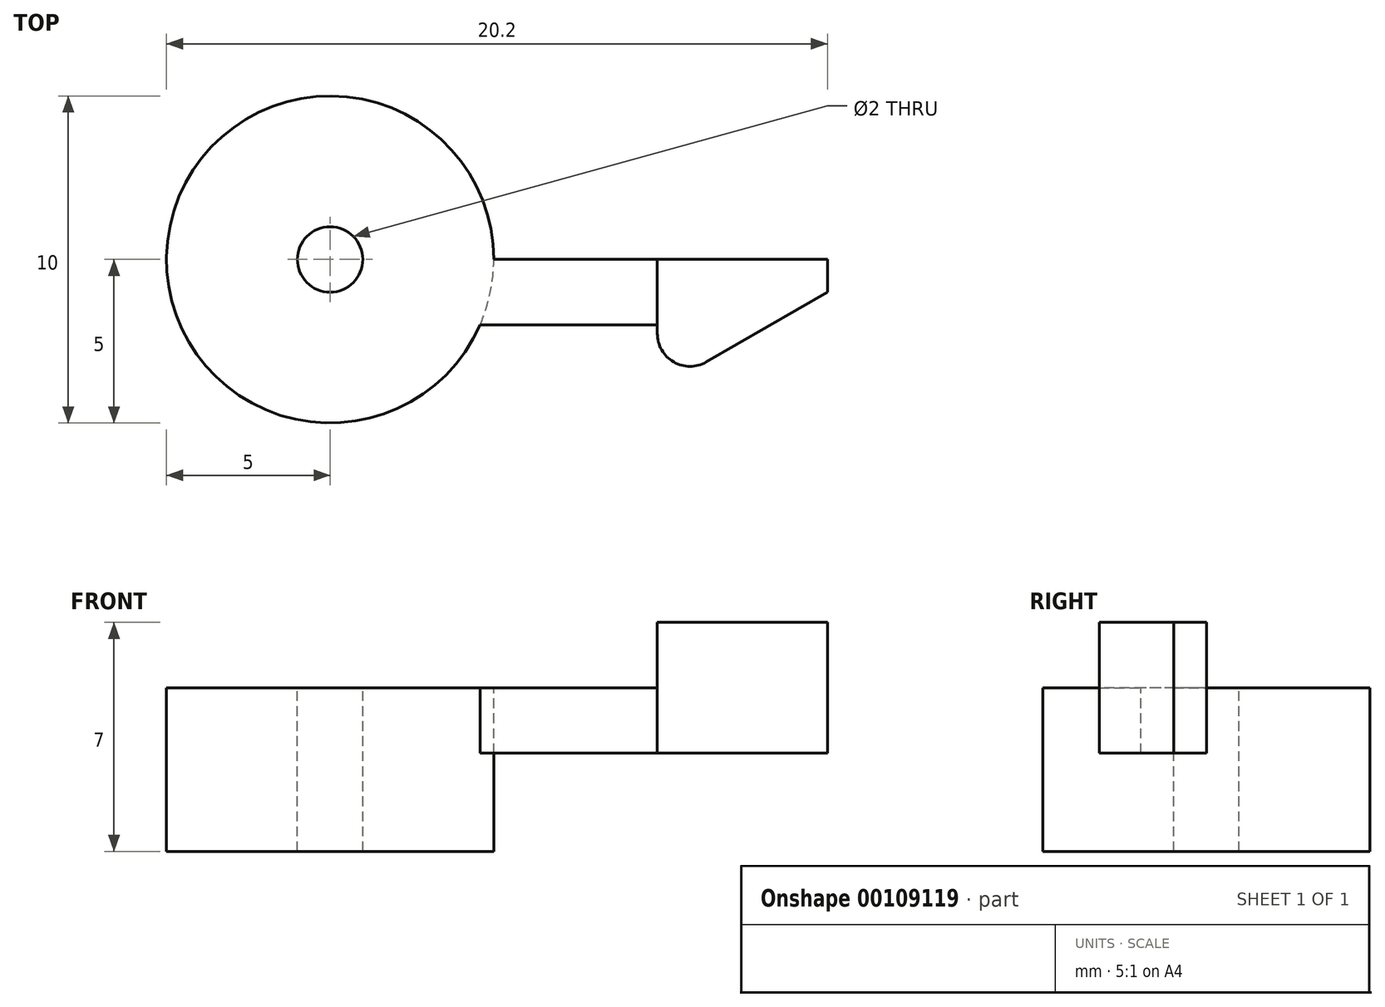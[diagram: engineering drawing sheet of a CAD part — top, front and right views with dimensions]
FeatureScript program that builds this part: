
annotation { "Feature Type Name" : "Feature", "Feature Type Description" : "" }
export const myFeature = defineFeature(function(context is Context, id is Id, definition is map)
    precondition{}
    {
        {
            var Q0;
            Q0=qCreatedBy(makeId("Top.planeOp"),FACE);
            var sketch = newSketch(context, id + "F0", { "sketchPlane" : qUnion([Q0])});
            skCircle(sketch, "E0", {"center": v(0, 0) * mm, "radius": 5 * mm});
            skLineSegment(sketch, "E1.MirrorCS", {"start": v(10, -2) * mm, "end": v(4.58, -2) * mm});
            skLineSegment(sketch, "E2.MirrorCS", {"start": v(10, -4) * mm, "end": v(15.2, -1) * mm});
            skLineSegment(sketch, "E3.MirrorCS", {"start": v(10, -2) * mm, "end": v(10, -4) * mm});
            skLineSegment(sketch, "E4.MirrorCS", {"start": v(15.2, -1) * mm, "end": v(15.2, 0) * mm});
            skLineSegment(sketch, "E5.MirrorCS", {"start": v(10, 0) * mm, "end": v(10, -2) * mm});
            skLineSegment(sketch, "E6", {"start": v(15.2, 0) * mm, "end": v(5, 0) * mm});
            skSolve(sketch);
        }
        {
            var Q0;
            {var subQ0=sQuery(id+"F0.wireOp",EDGE,"E0");var subQ1=makeQuery(id+"F0.imprint","INTERSECT",VERTEX,{"derivedFrom":[subQ0,sQuery(id+"F0.wireOp",EDGE,"E1.MirrorCS")]});Q0=makeQuery(id+"F0.imprint","IMPRINT",FACE,{"disambiguationData":[TD([[makeQuery(id+"F0.imprint","IMPRINT",EDGE,{"disambiguationData":[TD([[subQ1,1.0]])],"derivedFrom":subQ0}),1.0]])]});}
            extrude(context, id + "F1", {"entities" : qUnion([Q0]), "oppositeDirection" : true, "depth" : 5 * mm});
        }
        {
            var Q0;
            {var subQ0=sQuery(id+"F0.wireOp",EDGE,"E1.MirrorCS");Q0=makeQuery(id+"F0.imprint","IMPRINT",FACE,{"disambiguationData":[TD([[makeQuery(id+"F0.imprint","IMPRINT",EDGE,{"derivedFrom":subQ0}),-1.0]])]});}
            extrude(context, id + "F2", {"entities" : qUnion([Q0]), "operationType" : NewBodyOperationType.ADD, "oppositeDirection" : true, "depth" : 2 * mm});
        }
        {
            var Q0;
            Q0=makeQuery(id+"F0.imprint","IMPRINT",FACE,{"disambiguationData":[TD([[makeQuery(id+"F0.imprint","IMPRINT",EDGE,{"derivedFrom":sQuery(id+"F0.wireOp",EDGE,"E2.MirrorCS")}),1.0]])]});
            extrude(context, id + "F3", {"entities" : qUnion([Q0]), "operationType" : NewBodyOperationType.ADD, "endBound" : BoundingType.SYMMETRIC, "depth" : 4 * mm});
        }
        {
            var Q0;
            Q0=makeQuery(id+"F3.opExtrude","SWEPT_EDGE",EDGE,{"disambiguationData":[OSD([sQuery(id+"F0.wireOp",EDGE,"E2.MirrorCS"),sQuery(id+"F0.wireOp",EDGE,"E3.MirrorCS")])]});
            fillet(context, id + "F4", {"entities" : qUnion([Q0]), "radius" : 1 * mm, "tangentPropagation" : true, "allowEdgeOverflow" : false});
        }
        {
            var Q0;
            Q0=sQuery(id+"F0.wireOp",VERTEX,"E0.center");
            var Q1;
            Q1=makeQuery(id+"F1.opExtrude","SWEPT_BODY",BODY,{"disambiguationData":[OSD([sQuery(id+"F0.wireOp",EDGE,"E0")])]});
            hole(context, id + "F5", {"style" : HoleStyle.SIMPLE, "endStyle" : HoleEndStyle.THROUGH, "holeDiameter" : 2 * mm, "locations" : qUnion([Q0]), "scope" : qUnion([Q1]), "isTappedThrough" : true});
        }
    });
